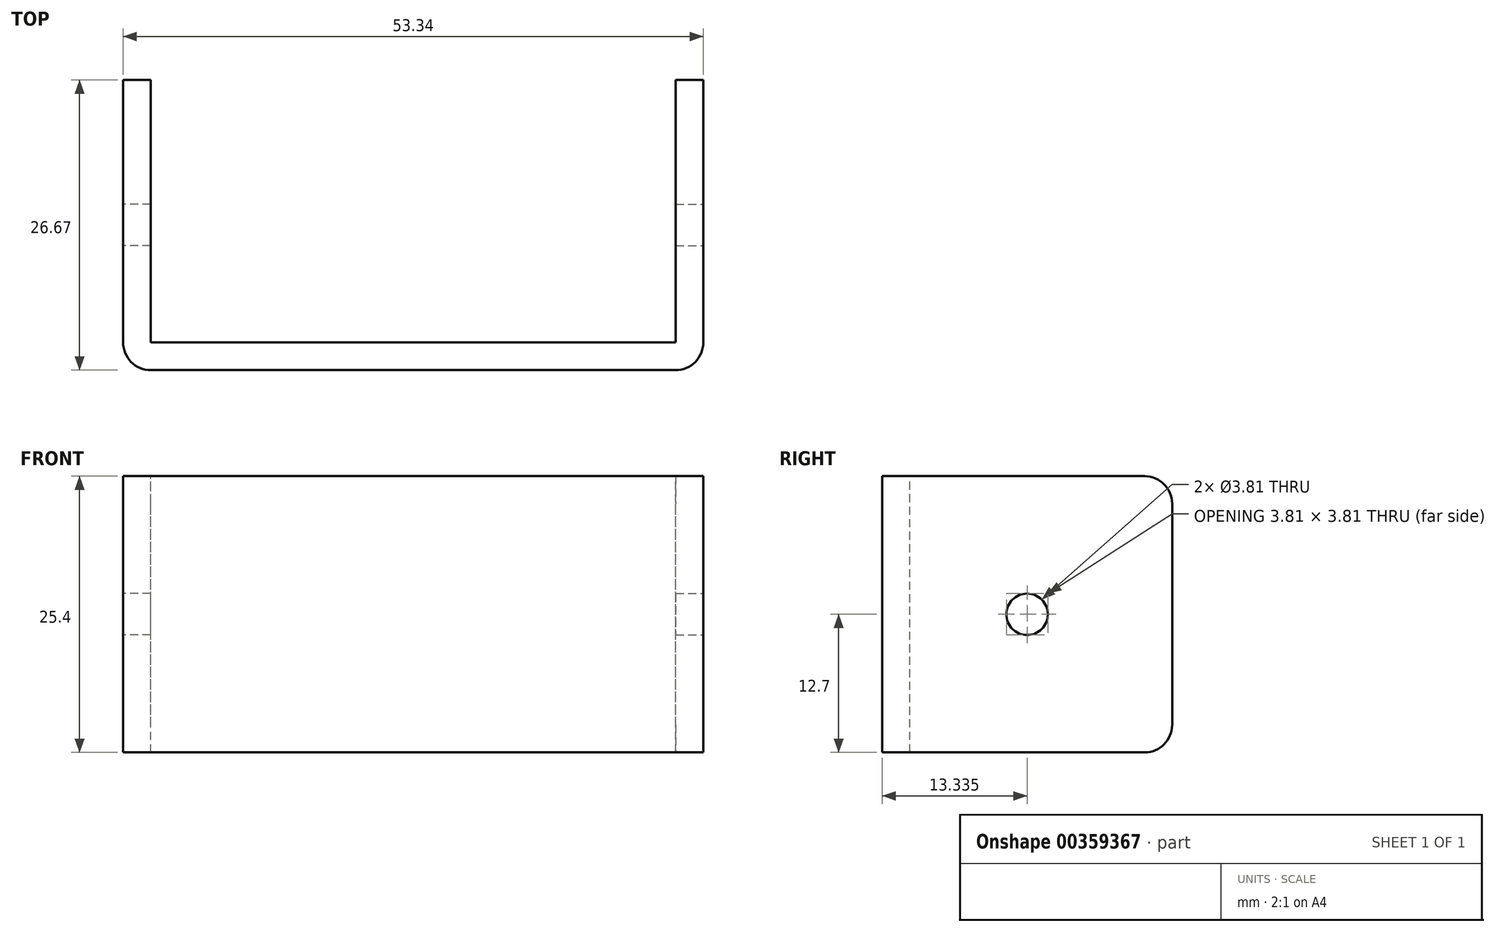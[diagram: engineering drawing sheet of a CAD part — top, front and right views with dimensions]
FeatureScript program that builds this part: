
annotation { "Feature Type Name" : "Feature", "Feature Type Description" : "" }
export const myFeature = defineFeature(function(context is Context, id is Id, definition is map)
    precondition{}
    {
        {
            var Q0;
            Q0=qCreatedBy(makeId("Top.planeOp"),FACE);
            var sketch = newSketch(context, id + "F0", { "sketchPlane" : qUnion([Q0])});
            skLineSegment(sketch, "E0", {"start": v(-50.8, 0) * mm, "end": v(-50.8, -25.4) * mm});
            skLineSegment(sketch, "E1", {"start": v(-50.8, -25.4) * mm, "end": v(0, -25.4) * mm});
            skLineSegment(sketch, "E2", {"start": v(0, -25.4) * mm, "end": v(0, 0) * mm});
            skSolve(sketch);
        }
        {
            var Q0;
            Q0=qCreatedBy(makeId("Front.planeOp"),FACE);
            var sketch = newSketch(context, id + "F1", { "sketchPlane" : qUnion([Q0])});
            skLineSegment(sketch, "E3.bottom", {"start": v(1.27, -12.7) * mm, "end": v(-1.27, -12.7) * mm});
            skLineSegment(sketch, "E3.top", {"start": v(1.27, 12.7) * mm, "end": v(-1.27, 12.7) * mm});
            skLineSegment(sketch, "E3.left", {"start": v(1.27, -12.7) * mm, "end": v(1.27, 12.7) * mm});
            skLineSegment(sketch, "E3.right", {"start": v(-1.27, -12.7) * mm, "end": v(-1.27, 12.7) * mm});
            skPoint(sketch, "E3.middle", {"position": v(0, 0) * mm});
            skSolve(sketch);
        }
        {
            var Q0;
            Q0 = qSketchRegion(id + "F1", true);
            var Q1;
            Q1=sQuery(id+"F0.wireOp",EDGE,"E0");
            var Q2;
            Q2=sQuery(id+"F0.wireOp",EDGE,"E1");
            var Q3;
            Q3=sQuery(id+"F0.wireOp",EDGE,"E2");
            sweep(context, id + "F2", {"profiles" : qUnion([Q0]), "path" : qUnion([Q1, Q2, Q3])});
        }
        {
            var Q0;
            Q0=makeQuery(id+"F2.opSweep","SWEPT_FACE",FACE,{"disambiguationData":[OSD([sQuery(id+"F0.wireOp",EDGE,"E2"),sQuery(id+"F1.wireOp",EDGE,"E3.left")])]});
            var sketch = newSketch(context, id + "F3", { "sketchPlane" : qUnion([Q0])});
            skCircle(sketch, "E4", {"center": v(-13.33, 0) * mm, "radius": 1.9 * mm});
            skPoint(sketch, "E4.centerSnap0", {"position": v(-13.34, 12.7) * mm});
            skSolve(sketch);
        }
        {
            var Q0;
            Q0=makeQuery(id+"F2.opSweep","SWEPT_FACE",FACE,{"disambiguationData":[OSD([sQuery(id+"F0.wireOp",EDGE,"E0"),sQuery(id+"F1.wireOp",EDGE,"E3.left")])]});
            var sketch = newSketch(context, id + "F4", { "sketchPlane" : qUnion([Q0])});
            skCircle(sketch, "E5", {"center": v(13.33, 0) * mm, "radius": 1.9 * mm});
            skPoint(sketch, "E5.centerSnap0", {"position": v(13.33, -12.7) * mm});
            skSolve(sketch);
        }
        {
            var Q0;
            Q0=makeQuery(id+"F3.imprint","IMPRINT",FACE,{"disambiguationData":[TD([[makeQuery(id+"F3.imprint","IMPRINT",EDGE,{"derivedFrom":sQuery(id+"F3.wireOp",EDGE,"E4")}),1.0]])]});
            extrude(context, id + "F5", {"entities" : qUnion([Q0]), "operationType" : NewBodyOperationType.REMOVE, "endBound" : BoundingType.UP_TO_NEXT, "oppositeDirection" : true, "depth" : 25.4 * mm});
        }
        {
            var Q0;
            Q0=makeQuery(id+"F4.imprint","IMPRINT",FACE,{"disambiguationData":[TD([[makeQuery(id+"F4.imprint","IMPRINT",EDGE,{"derivedFrom":sQuery(id+"F4.wireOp",EDGE,"E5")}),1.0]])]});
            extrude(context, id + "F6", {"entities" : qUnion([Q0]), "operationType" : NewBodyOperationType.REMOVE, "endBound" : BoundingType.UP_TO_NEXT, "oppositeDirection" : true, "depth" : 25.4 * mm});
        }
        {
            var Q0;
            Q0=makeQuery(id+"F2.opSweep","CAP_EDGE",EDGE,{"disambiguationData":[OSD([sQuery(id+"F0.wireOp",VERTEX,"E0.start"),sQuery(id+"F1.wireOp",EDGE,"E3.top")])],"isStart":false});
            var Q1;
            Q1=makeQuery(id+"F2.opSweep","CAP_EDGE",EDGE,{"disambiguationData":[OSD([sQuery(id+"F0.wireOp",VERTEX,"E0.start"),sQuery(id+"F1.wireOp",EDGE,"E3.bottom")])],"isStart":false});
            var Q2;
            Q2=makeQuery(id+"F2.opSweep","CAP_EDGE",EDGE,{"disambiguationData":[OSD([sQuery(id+"F0.wireOp",VERTEX,"E2.end"),sQuery(id+"F1.wireOp",EDGE,"E3.bottom")])],"isStart":true});
            var Q3;
            Q3=makeQuery(id+"F2.opSweep","CAP_EDGE",EDGE,{"disambiguationData":[OSD([sQuery(id+"F0.wireOp",VERTEX,"E2.end"),sQuery(id+"F1.wireOp",EDGE,"E3.top")])],"isStart":true});
            var Q4;
            Q4=makeQuery(id+"F2.opSweep","MID_CAP_EDGE",EDGE,{"disambiguationData":[OSD([sQuery(id+"F0.wireOp",VERTEX,"E2.start"),sQuery(id+"F1.wireOp",EDGE,"E3.left")])],"capPos":1.0});
            var Q5;
            Q5=makeQuery(id+"F2.opSweep","MID_CAP_EDGE",EDGE,{"disambiguationData":[OSD([sQuery(id+"F0.wireOp",VERTEX,"E1.start"),sQuery(id+"F1.wireOp",EDGE,"E3.left")])],"capPos":2.0});
            fillet(context, id + "F7", {"entities" : qUnion([Q0, Q1, Q2, Q3, Q4, Q5]), "radius" : 2.54 * mm, "tangentPropagation" : true, "allowEdgeOverflow" : false});
        }
    });
